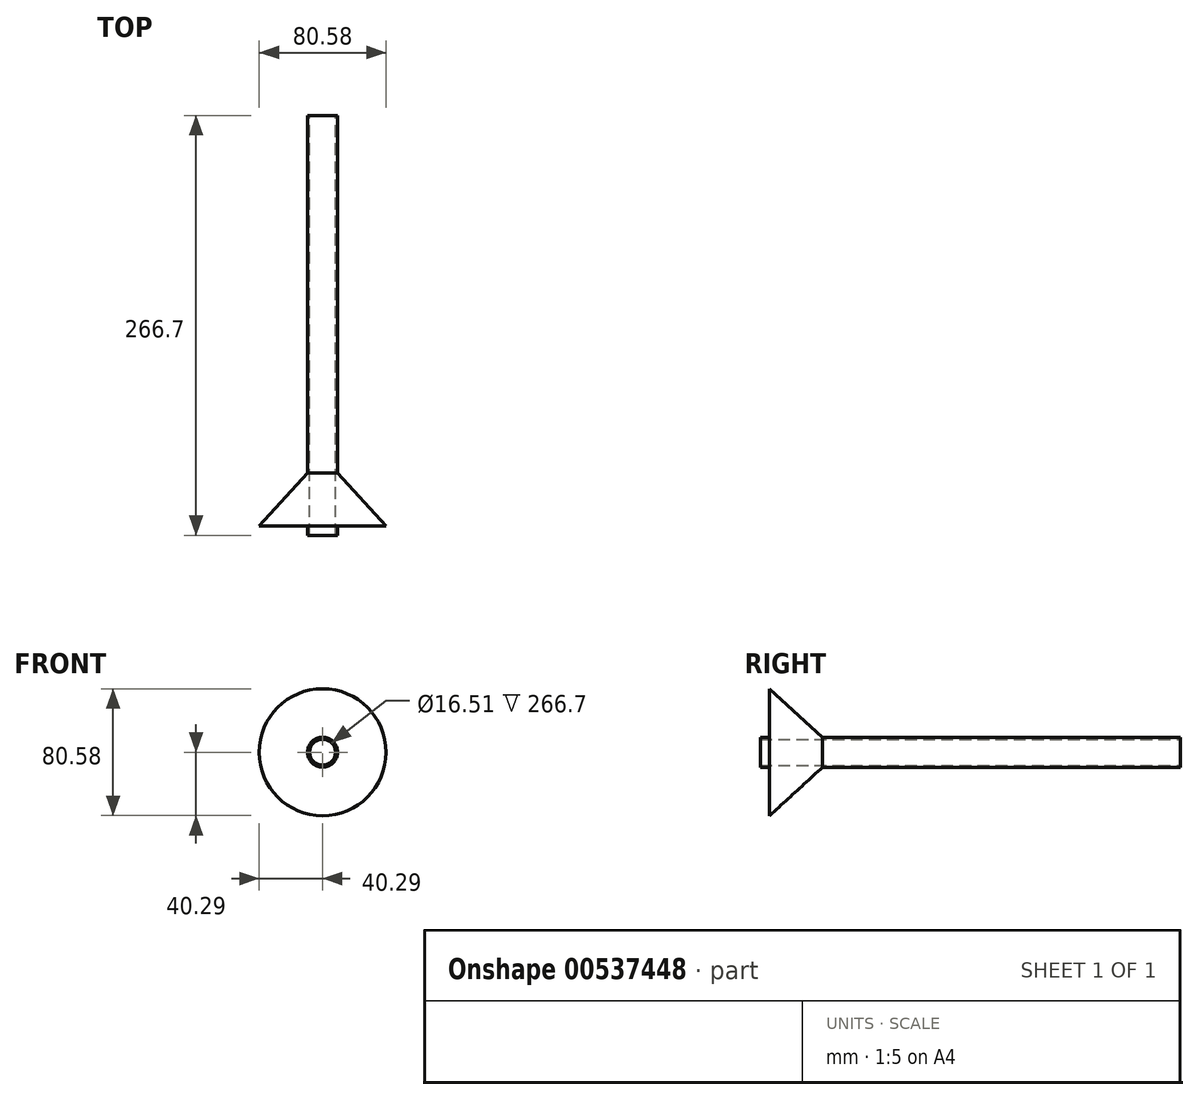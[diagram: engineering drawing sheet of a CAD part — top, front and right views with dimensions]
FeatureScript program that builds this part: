
annotation { "Feature Type Name" : "Feature", "Feature Type Description" : "" }
export const myFeature = defineFeature(function(context is Context, id is Id, definition is map)
    precondition{}
    {
        {
            var Q0;
            Q0=qCreatedBy(makeId("Front.planeOp"),FACE);
            var sketch = newSketch(context, id + "F0", { "sketchPlane" : qUnion([Q0])});
            skCircle(sketch, "E0", {"center": v(0, 0) * mm, "radius": 9.53 * mm});
            skCircle(sketch, "E1", {"center": v(0, 0) * mm, "radius": 8.26 * mm});
            skSolve(sketch);
        }
        {
            var Q0;
            Q0=makeQuery(id+"F0.imprint","IMPRINT",FACE,{"disambiguationData":[TD([[makeQuery(id+"F0.imprint","IMPRINT",EDGE,{"derivedFrom":sQuery(id+"F0.wireOp",EDGE,"E0")}),1.0]])]});
            extrude(context, id + "F1", {"entities" : qUnion([Q0]), "endBound" : BoundingType.SYMMETRIC, "depth" : 266.7 * mm, "offsetDistance" : 25.4 * mm});
        }
        {
            var Q0;
            Q0=qCreatedBy(makeId("Right.planeOp"),FACE);
            var sketch = newSketch(context, id + "F2", { "sketchPlane" : qUnion([Q0])});
            skPoint(sketch, "E2", {"position": v(-127.38, 9.53) * mm});
            skLineSegment(sketch, "E3", {"start": v(-127.38, 40.3) * mm, "end": v(-93.8, 9.53) * mm});
            skLineSegment(sketch, "E4", {"start": v(-93.8, 9.53) * mm, "end": v(-127.38, 9.53) * mm});
            skLineSegment(sketch, "E5", {"start": v(-127.38, 40.3) * mm, "end": v(-127.38, 9.53) * mm});
            skSolve(sketch);
        }
        {
            var Q0;
            Q0 = qSketchRegion(id + "F2", true);
            var Q1;
            Q1=makeQuery(id+"F1.opExtrude","SWEPT_FACE",FACE,{"disambiguationData":[OSD([sQuery(id+"F0.wireOp",EDGE,"E0")])]});
            revolve(context, id + "F3", {"operationType" : NewBodyOperationType.ADD, "entities" : qUnion([Q0]), "axis" : qUnion([Q1]), "revolveType" : RevolveType.FULL});
        }
    });
